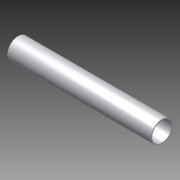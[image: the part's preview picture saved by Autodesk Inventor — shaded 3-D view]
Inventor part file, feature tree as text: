
AUTODESK INVENTOR PART (.ipt)
format: ipt  version: 2012 (Build 160160000, 160)  size: 77,824 bytes
history: native  units: mm
features: extrude x1, sketch x1
ambient origin geometry x8: Origin, YZ Plane, XZ Plane, XY Plane, X Axis, Y Axis, Z Axis, Center Point
bodies: Solid1 (feature_tree)
feature tree (2):
  extrude  "Extrusion1"  Depth=28.57mm
  sketch  "Sketch1"  dims[d0=31.75mm d1=28.57mm d2=212.0mm d3=0.0mm]
